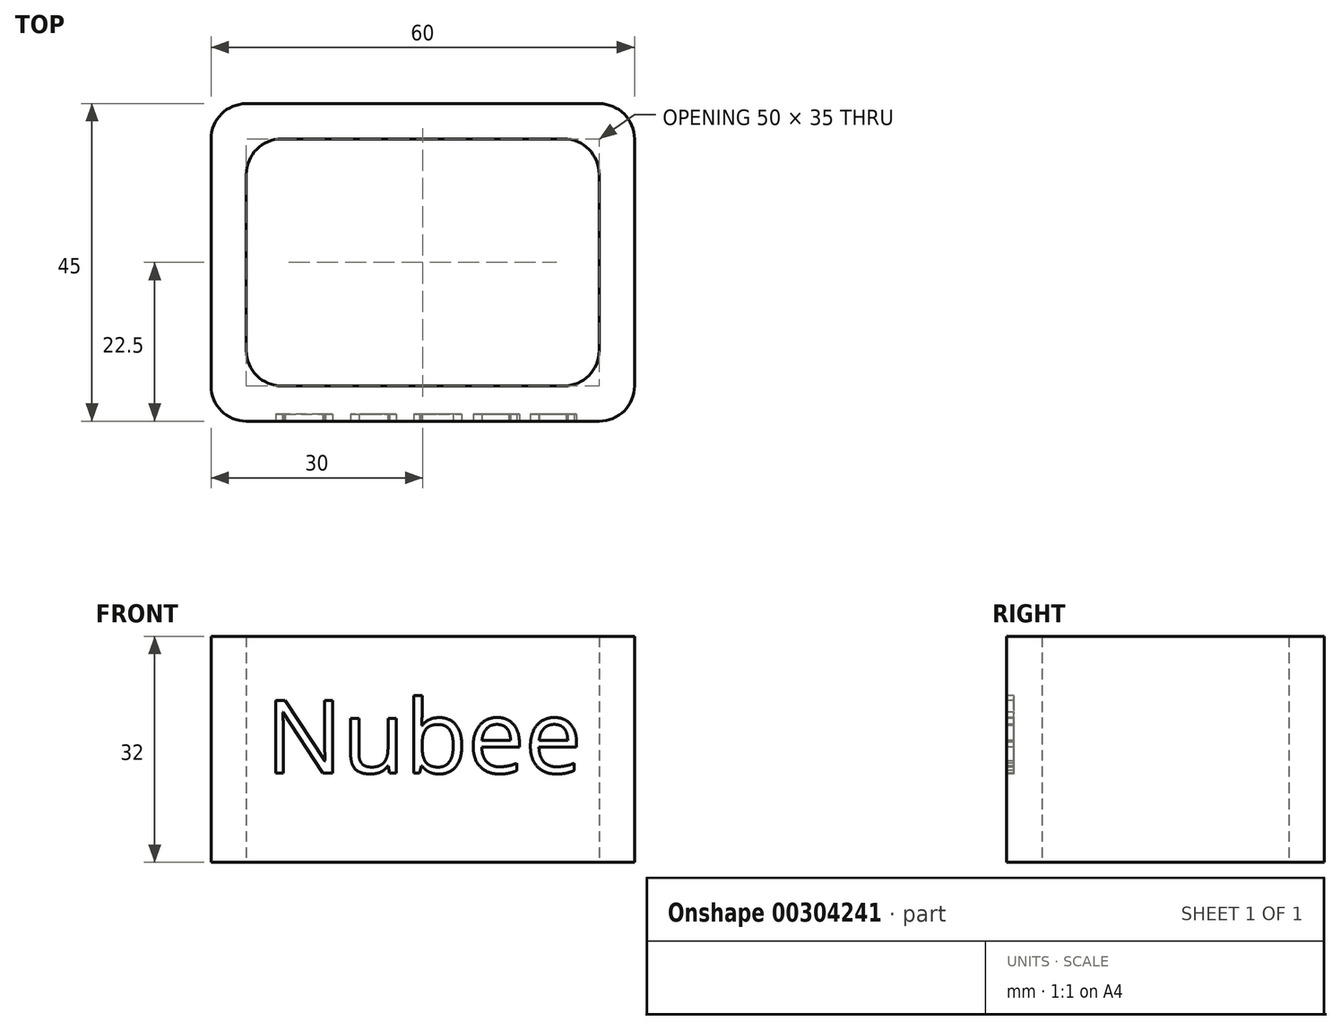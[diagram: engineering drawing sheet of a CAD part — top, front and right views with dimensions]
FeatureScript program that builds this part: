
annotation { "Feature Type Name" : "Feature", "Feature Type Description" : "" }
export const myFeature = defineFeature(function(context is Context, id is Id, definition is map)
    precondition{}
    {
        {
            var Q0;
            Q0=qCreatedBy(makeId("Top.planeOp"),FACE);
            var sketch = newSketch(context, id + "F0", { "sketchPlane" : qUnion([Q0])});
            skLineSegment(sketch, "E0.bottom", {"start": v(25, -17.5) * mm, "end": v(-25, -17.5) * mm});
            skLineSegment(sketch, "E0.top", {"start": v(25, 17.5) * mm, "end": v(-25, 17.5) * mm});
            skLineSegment(sketch, "E0.left", {"start": v(25, -17.5) * mm, "end": v(25, 17.5) * mm});
            skLineSegment(sketch, "E0.right", {"start": v(-25, -17.5) * mm, "end": v(-25, 17.5) * mm});
            skPoint(sketch, "E0.middle", {"position": v(0, 0) * mm});
            skPoint(sketch, "E1.middle", {"position": v(-1.81, 0) * mm});
            skLineSegment(sketch, "E2.0", {"start": v(30, 22.5) * mm, "end": v(-30, 22.5) * mm});
            skLineSegment(sketch, "E2.1", {"start": v(30, -22.5) * mm, "end": v(30, 22.5) * mm});
            skLineSegment(sketch, "E2.2", {"start": v(30, -22.5) * mm, "end": v(-30, -22.5) * mm});
            skLineSegment(sketch, "E2.3", {"start": v(-30, -22.5) * mm, "end": v(-30, 22.5) * mm});
            skSolve(sketch);
        }
        {
            var Q0;
            Q0=makeQuery(id+"F0.imprint","IMPRINT",FACE,{"disambiguationData":[TD([[makeQuery(id+"F0.imprint","IMPRINT",EDGE,{"derivedFrom":sQuery(id+"F0.wireOp",EDGE,"E0.bottom")}),1.0]])]});
            extrude(context, id + "F1", {"entities" : qUnion([Q0]), "endBound" : BoundingType.SYMMETRIC, "depth" : 25 * mm});
        }
        {
            var Q0;
            Q0=makeQuery(id+"F1.opExtrude","SWEPT_EDGE",EDGE,{"disambiguationData":[OSD([sQuery(id+"F0.wireOp",EDGE,"E0.top"),sQuery(id+"F0.wireOp",EDGE,"E0.right")])]});
            var Q1;
            Q1=makeQuery(id+"F1.opExtrude","SWEPT_EDGE",EDGE,{"disambiguationData":[OSD([sQuery(id+"F0.wireOp",EDGE,"E0.bottom"),sQuery(id+"F0.wireOp",EDGE,"E0.right")])]});
            var Q2;
            Q2=makeQuery(id+"F1.opExtrude","SWEPT_EDGE",EDGE,{"disambiguationData":[OSD([sQuery(id+"F0.wireOp",EDGE,"E0.bottom"),sQuery(id+"F0.wireOp",EDGE,"E0.left")])]});
            fillet(context, id + "F2", {"entities" : qUnion([Q0, Q1, Q2]), "radius" : 5 * mm, "tangentPropagation" : true, "allowEdgeOverflow" : false});
        }
        {
            var Q0;
            Q0=makeQuery(id+"F1.opExtrude","SWEPT_EDGE",EDGE,{"disambiguationData":[OSD([sQuery(id+"F0.wireOp",EDGE,"E0.top"),sQuery(id+"F0.wireOp",EDGE,"E0.left")])]});
            var Q1;
            Q1=makeQuery(id+"F1.opExtrude","SWEPT_EDGE",EDGE,{"disambiguationData":[OSD([sQuery(id+"F0.wireOp",EDGE,"E2.1"),sQuery(id+"F0.wireOp",EDGE,"E2.2")])]});
            var Q2;
            Q2=makeQuery(id+"F1.opExtrude","SWEPT_EDGE",EDGE,{"disambiguationData":[OSD([sQuery(id+"F0.wireOp",EDGE,"E2.2"),sQuery(id+"F0.wireOp",EDGE,"E2.3")])]});
            var Q3;
            Q3=makeQuery(id+"F1.opExtrude","SWEPT_EDGE",EDGE,{"disambiguationData":[OSD([sQuery(id+"F0.wireOp",EDGE,"E2.0"),sQuery(id+"F0.wireOp",EDGE,"E2.3")])]});
            var Q4;
            Q4=makeQuery(id+"F1.opExtrude","SWEPT_EDGE",EDGE,{"disambiguationData":[OSD([sQuery(id+"F0.wireOp",EDGE,"E2.0"),sQuery(id+"F0.wireOp",EDGE,"E2.1")])]});
            fillet(context, id + "F3", {"entities" : qUnion([Q0, Q1, Q2, Q3, Q4]), "radius" : 5 * mm, "tangentPropagation" : true, "allowEdgeOverflow" : false});
        }
        {
            var Q0;
            Q0=makeQuery(id+"F1.opExtrude","CAP_FACE",FACE,{"disambiguationData":[OSD([sQuery(id+"F0.wireOp",EDGE,"E0.bottom"),sQuery(id+"F0.wireOp",EDGE,"E0.top"),sQuery(id+"F0.wireOp",EDGE,"E0.left"),sQuery(id+"F0.wireOp",EDGE,"E0.right"),sQuery(id+"F0.wireOp",EDGE,"E2.0"),sQuery(id+"F0.wireOp",EDGE,"E2.1"),sQuery(id+"F0.wireOp",EDGE,"E2.2"),sQuery(id+"F0.wireOp",EDGE,"E2.3")])],"isStart":true});
            extrude(context, id + "F4", {"entities" : qUnion([Q0]), "operationType" : NewBodyOperationType.ADD, "endBound" : BoundingType.SYMMETRIC, "depth" : 10 * mm});
        }
        {
            var Q0;
            Q0=makeQuery(id+"F4.opExtrude","CAP_FACE",FACE,{"disambiguationData":[OSD([sQuery(id+"F0.wireOp",EDGE,"E0.bottom"),sQuery(id+"F0.wireOp",EDGE,"E0.top"),sQuery(id+"F0.wireOp",EDGE,"E0.left"),sQuery(id+"F0.wireOp",EDGE,"E0.right"),sQuery(id+"F0.wireOp",EDGE,"E2.0"),sQuery(id+"F0.wireOp",EDGE,"E2.1"),sQuery(id+"F0.wireOp",EDGE,"E2.2"),sQuery(id+"F0.wireOp",EDGE,"E2.3")])],"isStart":false});
            extrude(context, id + "F5", {"entities" : qUnion([Q0]), "operationType" : NewBodyOperationType.ADD, "endBound" : BoundingType.SYMMETRIC, "depth" : 2 * mm});
        }
        {
            var Q0;
            {var subQ0=sQuery(id+"F0.wireOp",EDGE,"E2.0");Q0=makeQuery(id+"F5.boolean.opBoolean","MERGE",FACE,{"derivedFrom":[makeQuery(id+"F4.boolean.opBoolean","MERGE",FACE,{"derivedFrom":[makeQuery(id+"F1.opExtrude","SWEPT_FACE",FACE,{"disambiguationData":[OSD([subQ0])]}),makeQuery(id+"F4.opExtrude","SWEPT_FACE",FACE,{"disambiguationData":[OSD([subQ0])]})]}),makeQuery(id+"F5.opExtrude","SWEPT_FACE",FACE,{"disambiguationData":[OSD([subQ0])]})]});}
            var sketch = newSketch(context, id + "F6", { "sketchPlane" : qUnion([Q0])});
            skLineSegment(sketch, "E3.bottom", {"start": v(12.5, -6.98) * mm, "end": v(-12.5, -6.98) * mm});
            skLineSegment(sketch, "E3.top", {"start": v(12.5, 6.98) * mm, "end": v(-12.5, 6.98) * mm});
            skLineSegment(sketch, "E3.left", {"start": v(12.5, -6.98) * mm, "end": v(12.5, 6.98) * mm});
            skLineSegment(sketch, "E3.right", {"start": v(-12.5, -6.98) * mm, "end": v(-12.5, 6.98) * mm});
            skPoint(sketch, "E3.middle", {"position": v(0, 0) * mm});
            skSolve(sketch);
        }
        {
            var Q0;
            Q0=makeQuery(id+"F1.opExtrude","CAP_FACE",FACE,{"disambiguationData":[OSD([sQuery(id+"F0.wireOp",EDGE,"E0.bottom"),sQuery(id+"F0.wireOp",EDGE,"E0.top"),sQuery(id+"F0.wireOp",EDGE,"E0.left"),sQuery(id+"F0.wireOp",EDGE,"E0.right"),sQuery(id+"F0.wireOp",EDGE,"E2.0"),sQuery(id+"F0.wireOp",EDGE,"E2.1"),sQuery(id+"F0.wireOp",EDGE,"E2.2"),sQuery(id+"F0.wireOp",EDGE,"E2.3")])],"isStart":false});
            extrude(context, id + "F7", {"entities" : qUnion([Q0]), "operationType" : NewBodyOperationType.ADD, "depth" : 1 * mm});
        }
        {
            var Q0;
            {var subQ0=sQuery(id+"F0.wireOp",EDGE,"E2.2");Q0=makeQuery(id+"F7.boolean.opBoolean","MERGE",FACE,{"derivedFrom":[makeQuery(id+"F5.boolean.opBoolean","MERGE",FACE,{"derivedFrom":[makeQuery(id+"F4.boolean.opBoolean","MERGE",FACE,{"derivedFrom":[makeQuery(id+"F1.opExtrude","SWEPT_FACE",FACE,{"disambiguationData":[OSD([subQ0])]}),makeQuery(id+"F4.opExtrude","SWEPT_FACE",FACE,{"disambiguationData":[OSD([subQ0])]})]}),makeQuery(id+"F5.opExtrude","SWEPT_FACE",FACE,{"disambiguationData":[OSD([subQ0])]})]}),makeQuery(id+"F7.opExtrude","SWEPT_FACE",FACE,{"disambiguationData":[OSD([subQ0])]})]});}
            var sketch = newSketch(context, id + "F8", { "sketchPlane" : qUnion([Q0])});
            skText(sketch, "E4", { "text": "Nubee", "fontName": "OpenSans-Regular.ttf"});
            const initialGuessF8  = {"E4": [-0.02227, -0.00586, 1, 0, 0.0104]};
            skSetInitialGuess(sketch, initialGuessF8);
            skSolve(sketch);
        }
        {
            var Q0;
            Q0 = qSketchRegion(id + "F8", true);
            extrude(context, id + "F9", {"entities" : qUnion([Q0]), "operationType" : NewBodyOperationType.REMOVE, "oppositeDirection" : true, "depth" : 1 * mm});
        }
    });
